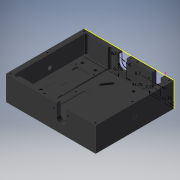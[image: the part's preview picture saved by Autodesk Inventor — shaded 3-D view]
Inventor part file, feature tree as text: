
AUTODESK INVENTOR PART (.ipt)
format: ipt  version: 2019.4 (Build 234330000, 330)  size: 552,448 bytes
history: native  units: mm
features: sketch x21, extrude x19, hole x16, pattern_linear x3
ambient origin geometry x8: Origin, YZ Plane, XZ Plane, XY Plane, X Axis, Y Axis, Z Axis, Center Point
bodies: Solid1 (feature_tree)
feature tree (59):
  extrude  "Extrusion1"  Depth=79.0mm
  sketch  "Sketch2"  dims[d2=21.51mm d3=0.0mm d4=4.0mm]
  extrude  "Extrusion2"  Depth=4.0mm
  extrude  "Extrusion3"  Depth=4.0mm
  sketch  "Sketch3"  dims[d5=4.0mm d6=4.0mm]
  hole  "Hole1"  [1 undecoded]
  hole  "Hole2"  [1 undecoded]
  sketch  "Sketch4"  dims[d7=50.5mm d8=4.0mm]
  hole  "Hole3"  [1 undecoded]
  hole  "Hole4"  [1 undecoded]
  hole  "Hole5"  [1 undecoded]
  extrude  "Extrusion4"  Depth=4.0mm
  sketch  "Sketch7"  dims[d15=4.0mm d16=2.0mm]
  extrude  "Extrusion5"  Depth=4.0mm
  extrude  "Extrusion6"  Depth=15.91mm
  sketch  "Sketch8"  dims[d17=4.0mm d18=4.0mm]
  sketch  "Sketch9"  dims[d19=2.0mm d20=4.0mm]
  sketch  "Sketch10"  dims[d21=2.0mm d22=4.0mm]
  hole  "Hole9"  [1 undecoded]
  pattern_linear  "Rectangular Pattern2"  Spacing1=2.5mm  [1 undecoded]
  hole  "Hole10"  [1 undecoded]
  pattern_linear  "Rectangular Pattern3"  Spacing1=8.2mm  [1 undecoded]
  sketch  "Sketch12"  dims[d24=4.0mm d25=2.5mm d26=4.0mm d27=2.0mm d28=90.0deg d29=17.51mm d30=0.0mm]
  extrude  "Extrusion9"  Depth=4.0mm TaperAngle=0.0deg
  extrude  "Extrusion10"  Depth=11.75mm
  extrude  "Extrusion11"  Depth=0.75mm
  extrude  "Extrusion13"  Depth=8.2mm
  sketch  "Sketch13"  dims[d31=4.0mm d32=2.5mm d33=4.0mm d34=2.0mm d35=90.0deg d36=15.91mm d37=0.0mm d38=4.5mm]
  extrude  "Extrusion14"  Depth=8.5mm
  extrude  "Extrusion15"  Depth=4.0mm TaperAngle=0.0deg
  extrude  "Extrusion17"  Depth=4.0mm TaperAngle=0.0deg
  extrude  "Extrusion18"  Depth=47.0mm
  extrude  "Extrusion19"  Depth=47.0mm
  extrude  "Extrusion20"  Depth=53.5mm
  extrude  "Extrusion22"  Depth=0.75mm
  extrude  "Extrusion23"  Depth=0.75mm
  hole  "Hole11"  [1 undecoded]
  extrude  "Extrusion26"  Depth=0.75mm
  sketch  "Sketch18"  dims[d42=2.5mm]
  hole  "Hole12"  [1 undecoded]
  pattern_linear  "Rectangular Pattern4"  Spacing1=6.05mm  [1 undecoded]
  hole  "Hole13"  [1 undecoded]
  hole  "Hole14"  [1 undecoded]
  hole  "Hole15"  [1 undecoded]
  hole  "Hole16"  [1 undecoded]
  hole  "Hole17"  [1 undecoded]
  hole  "Hole18"  [1 undecoded]
  hole  "Hole19"  [1 undecoded]
  sketch  "Sketch1"  dims[d0=69.0mm d1=79.0mm]
  sketch  "Sketch5"  dims[d9=17.51mm d10=0.0mm d11=15.91mm d12=0.0mm]
  sketch  "Sketch6"  dims[d13=4.0mm d14=2.0mm]
  sketch  "Sketch14"  dims[d39=4.75mm d40=22.75mm]
  sketch  "Sketch17"  dims[d41=56.25mm]
  sketch  "Sketch19"  dims[d43=3.54mm]
  sketch  "Sketch20"  dims[d44=2.5mm]
  sketch  "Sketch21"  dims[d45=26.96mm]
  sketch  "Sketch22"  dims[d46=1.694mm d47=2.0mm d48=4.0mm d49=2.0mm d50=90.0deg d51=3.0mm d52=0.0mm]
  sketch  "Sketch23"  dims[d53=2.642mm d54=7.01mm d55=4.0mm d56=2.0mm d57=90.0deg d58=10.979mm d59=0.0mm]
  sketch  "Sketch24"  dims[d60=2.75mm d61=2.5mm d62=1.694mm d63=2.0mm d64=4.0mm d65=2.0mm d66=90.0deg d67=3.0mm d68=0.0mm d69=30.55mm d70=8.2mm d72=4.0mm d73=0.0mm d74=11.75mm d75=41.75mm d76=8.2mm d78=8.5mm d80=4.0mm d81=0.0mm d82=4.0mm d83=0.0mm d104=47.0mm d105=47.0mm d106=53.5mm d107=33.332mm d108=42.215mm d109=37.75mm d117=19.6mm d118=23.0mm d119=6.05mm d120=6.05mm d151=41.57mm d152=44.11mm d153=46.57mm d154=50.46mm d155=8.29mm d156=3.53mm d157=5.75mm d158=7.02mm d169=1.75mm d170=2.0mm d171=4.0mm d172=2.0mm d173=90.0deg d174=2.0mm d175=0.0mm d176=20.0mm d178=15.87mm d179=3.75mm d180=2.0mm d181=4.0mm d182=2.0mm d183=90.0deg d184=2.0mm d185=0.0mm d186=20.0mm d188=11.43mm d197=18.0mm d198=21.758mm d199=2.62mm d200=2.62mm d201=2.0mm d202=2.0mm d203=22.66mm d204=27.362mm d205=19.4mm d206=19.4mm d207=2.0mm d208=2.0mm d209=5.75mm d210=14.45mm d211=30.96mm d212=30.96mm d213=2.0mm d214=2.0mm d221=0.75mm d222=0.5mm d223=0.0mm d224=0.5mm d225=0.0mm d226=0.5mm d227=0.0mm d230=0.5mm d231=0.0mm d256=0.5mm d257=0.0mm d258=0.5mm d259=0.0mm d270=3.0mm d271=3.0mm d272=3.0mm d273=2.0mm d274=0.0mm d275=2.0mm d276=0.0mm d277=2.0mm d278=0.0mm d279=2.5mm d280=2.5mm d283=2.0mm d284=0.0mm d287=0.75mm d288=2.0mm d289=0.0mm d293=0.75mm d294=1.0mm d295=0.0mm d302=4.0mm d303=6.0mm d304=4.0mm d305=2.0mm d306=90.0deg d307=17.51mm d308=0.0mm d309=14.5mm d310=2.0mm d311=0.0mm d312=2.0mm d313=2.0mm d316=1.694mm d317=4.369mm d318=4.0mm d319=2.0mm d320=90.0deg d321=6.637mm d322=0.0mm d323=20.0mm d325=75.0mm d326=30.0mm d328=32.5mm d329=2.5mm d330=2.5mm d331=3.0mm d332=3.0mm d333=1.694mm d334=4.369mm d335=4.0mm d336=2.0mm d337=90.0deg d338=6.637mm d339=0.0mm d340=4.0mm d341=4.0mm d342=5.0mm d343=5.0mm d344=2.0mm d345=2.0mm d346=1.694mm d347=4.369mm d348=4.0mm d349=2.0mm d350=90.0deg d351=6.637mm d352=0.0mm d353=5.0mm d354=2.0mm d355=5.0mm d356=2.0mm d357=1.694mm d358=4.369mm d359=4.0mm d360=2.0mm d361=90.0deg d362=6.637mm d363=0.0mm d364=7.13mm d365=7.13mm d366=9.732mm d368=2.0mm d369=2.0mm d370=30.0mm d371=1.694mm d372=4.369mm d373=4.0mm d374=2.0mm d375=90.0deg d376=6.637mm d377=0.0mm d381=1.0mm d382=34.5mm d383=10.755mm d384=3.302mm d385=8.331mm d386=4.0mm d387=2.0mm d388=90.0deg d389=12.3mm d390=0.0mm d391=8.0mm d392=15.0mm d393=3.302mm d394=8.331mm d395=4.0mm d396=2.0mm d397=90.0deg d398=12.3mm d399=0.0mm d400=8.0mm d401=15.0mm d402=3.302mm d403=8.331mm d404=4.0mm d405=2.0mm d406=90.0deg d407=12.3mm d408=0.0mm d409=47.06mm d411=1.25mm d412=9.0mm d413=9.0mm d414=9.0mm d415=9.0mm d416=17.55mm d417=3.55mm d418=1.0mm d419=5.4mm d420=17.5mm d421=17.4mm d422=11.5mm d423=7.45mm d424=11.75mm d425=18.0mm d426=27.5mm d427=1.0mm d428=1.0mm d429=1.0mm d430=32.0mm d159=1.0mm d160=1.0mm d161=1.0mm d162=0.15mm d163=0.25mm d164=0.375mm d165=14.3117mm d166=0.75mm d167=20.594885mm d168=0.0625mm d324=20.594885mm d327=0.375mm]
note: 19 required parameter values undecoded (feature->parameter linkage not recoverable at this tier; creation-order binding heuristic only, values carry confidence <= 0.55)
